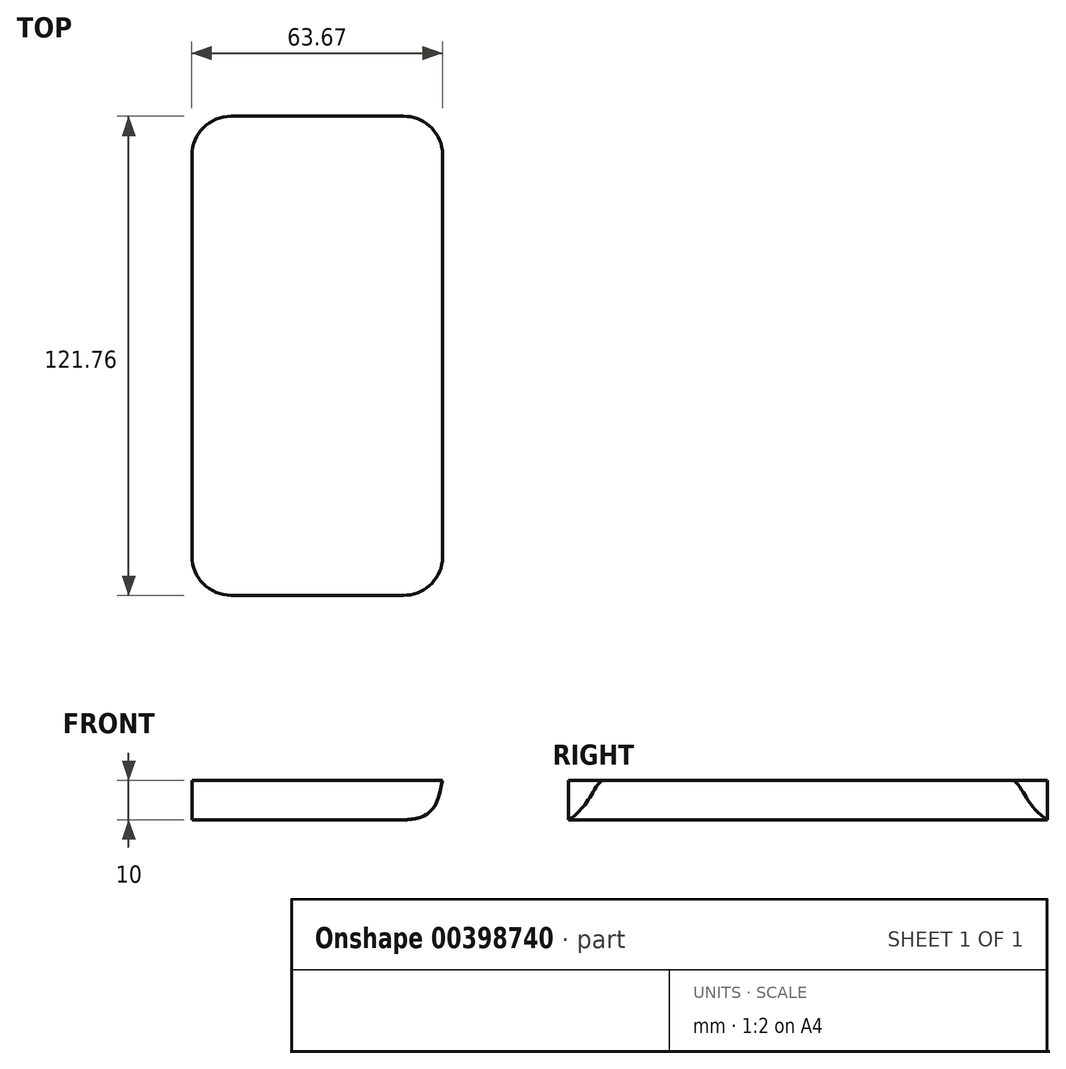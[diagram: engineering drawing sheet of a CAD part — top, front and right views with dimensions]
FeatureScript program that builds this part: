
annotation { "Feature Type Name" : "Feature", "Feature Type Description" : "" }
export const myFeature = defineFeature(function(context is Context, id is Id, definition is map)
    precondition{}
    {
        {
            var Q0;
            Q0=qCreatedBy(makeId("Top.planeOp"),FACE);
            var sketch = newSketch(context, id + "F0", { "sketchPlane" : qUnion([Q0])});
            skLineSegment(sketch, "E0.bottom", {"start": v(-21.87, 60.88) * mm, "end": v(21.87, 60.88) * mm});
            skLineSegment(sketch, "E0.top", {"start": v(-21.88, -60.88) * mm, "end": v(21.87, -60.88) * mm});
            skLineSegment(sketch, "E0.left", {"start": v(-31.88, 50.88) * mm, "end": v(-31.88, -50.88) * mm});
            skLineSegment(sketch, "E0.right", {"start": v(31.88, 50.88) * mm, "end": v(31.87, -50.88) * mm});
            skPoint(sketch, "E0.middle", {"position": v(0, 0) * mm});
            skPoint(sketch, "E1.visualSharp", {"position": v(-31.87, 60.88) * mm});
            skArc(sketch, "E1.filletArc", {"start": v(-21.87, 60.88) * mm, "mid": v(-28.95, 57.95) * mm, "end": v(-31.87, 50.88) * mm});
            skPoint(sketch, "E2.visualSharp", {"position": v(31.88, 60.88) * mm});
            skArc(sketch, "E2.filletArc", {"start": v(31.87, 50.88) * mm, "mid": v(28.95, 57.95) * mm, "end": v(21.87, 60.88) * mm});
            skPoint(sketch, "E3.visualSharp", {"position": v(31.87, -60.88) * mm});
            skArc(sketch, "E3.filletArc", {"start": v(21.87, -60.88) * mm, "mid": v(28.95, -57.95) * mm, "end": v(31.87, -50.88) * mm});
            skPoint(sketch, "E4.visualSharp", {"position": v(-31.88, -60.88) * mm});
            skArc(sketch, "E4.filletArc", {"start": v(-31.88, -50.88) * mm, "mid": v(-28.95, -57.95) * mm, "end": v(-21.88, -60.88) * mm});
            skSolve(sketch);
        }
        {
            var Q0;
            Q0 = qSketchRegion(id + "F0", true);
            extrude(context, id + "F1", {"entities" : qUnion([Q0]), "depth" : 10 * mm});
        }
        {
            var Q0;
            Q0=makeQuery(id+"F1.opExtrude","SWEPT_FACE",FACE,{"disambiguationData":[OSD([sQuery(id+"F0.wireOp",EDGE,"E0.top")])]});
            var sketch = newSketch(context, id + "F2", { "sketchPlane" : qUnion([Q0])});
            skFitSpline(sketch, "E5", {"points": [v(21.87, 0) * mm, v(31.93, 10.64) * mm], "startDerivative": vector(26.38, 0) * mm, "endDerivative": vector(3.7, 15.64) * mm});
            skLineSegment(sketch, "E6", {"start": v(31.93, 10.64) * mm, "end": v(31.93, 0) * mm});
            skLineSegment(sketch, "E7", {"start": v(31.93, 0) * mm, "end": v(21.87, 0) * mm});
            skLineSegment(sketch, "E8", {"start": v(0, 0) * mm, "end": v(0, 10) * mm});
            skLineSegment(sketch, "E9", {"start": v(21.87, 0) * mm, "end": v(0, 0) * mm});
            skSolve(sketch);
        }
        {
            var Q0;
            Q0=makeQuery(id+"F2.imprint","IMPRINT",FACE,{"disambiguationData":[TD([[makeQuery(id+"F2.imprint","IMPRINT",EDGE,{"derivedFrom":sQuery(id+"F2.wireOp",EDGE,"E5")}),-1.0]])]});
            extrude(context, id + "F3", {"entities" : qUnion([Q0]), "operationType" : NewBodyOperationType.REMOVE, "endBound" : BoundingType.SYMMETRIC, "oppositeDirection" : true, "depth" : 247.6 * mm});
        }
    });
